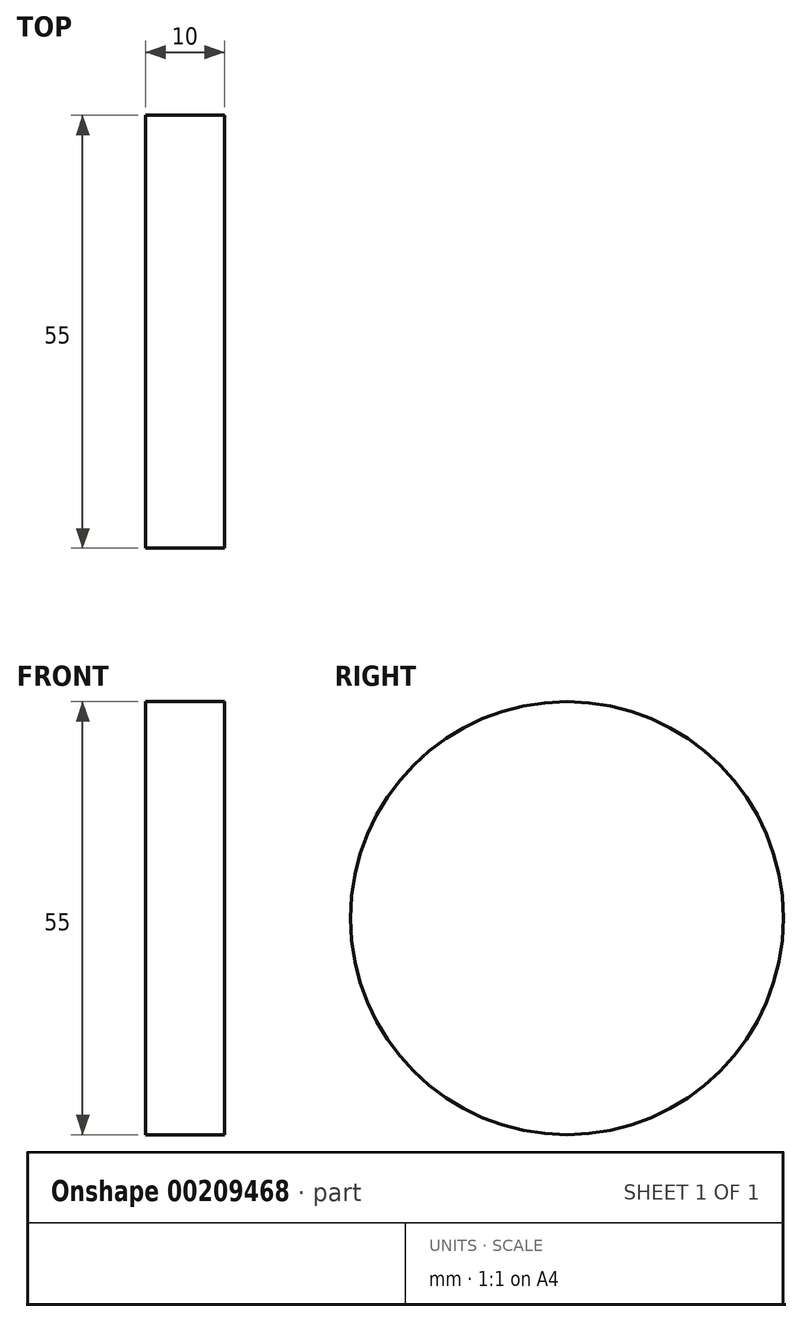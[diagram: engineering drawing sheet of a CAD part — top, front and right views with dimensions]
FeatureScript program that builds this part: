
annotation { "Feature Type Name" : "Feature", "Feature Type Description" : "" }
export const myFeature = defineFeature(function(context is Context, id is Id, definition is map)
    precondition{}
    {
        {
            var Q0;
            Q0=qCreatedBy(makeId("Right.planeOp"),FACE);
            var sketch = newSketch(context, id + "F0", { "sketchPlane" : qUnion([Q0])});
            skCircle(sketch, "E0", {"center": v(0, 0) * mm, "radius": 27.5 * mm});
            skSolve(sketch);
        }
        {
            var Q0;
            Q0=makeQuery(id+"F0.imprint","IMPRINT",FACE,{"disambiguationData":[TD([[makeQuery(id+"F0.imprint","IMPRINT",EDGE,{"derivedFrom":sQuery(id+"F0.wireOp",EDGE,"E0")}),1.0]])]});
            extrude(context, id + "F1", {"entities" : qUnion([Q0]), "depth" : 10 * mm});
        }
    });
